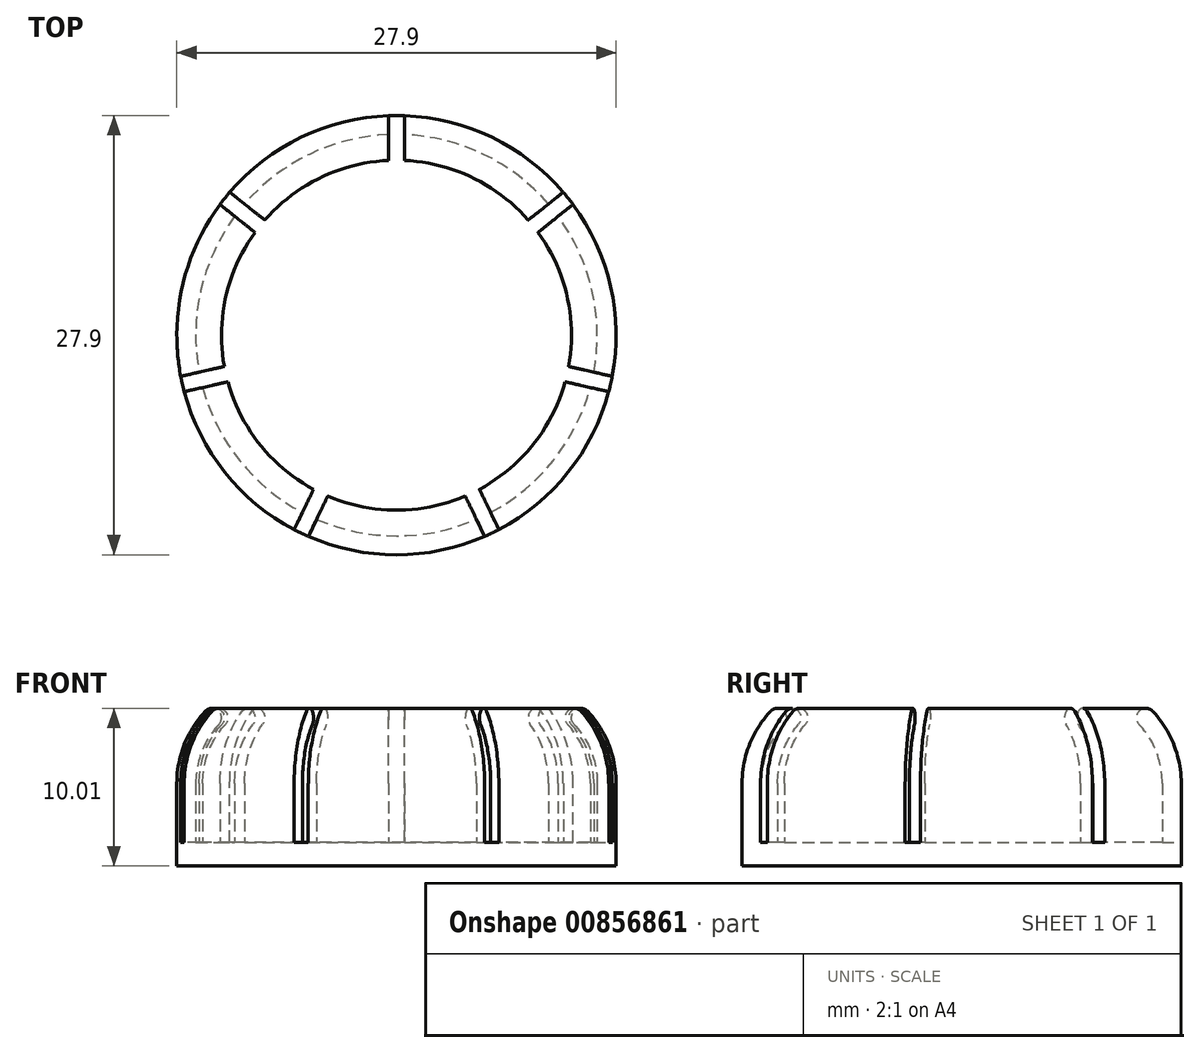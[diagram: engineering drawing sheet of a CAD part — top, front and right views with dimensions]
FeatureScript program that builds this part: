
annotation { "Feature Type Name" : "Feature", "Feature Type Description" : "" }
export const myFeature = defineFeature(function(context is Context, id is Id, definition is map)
    precondition{}
    {
        {
            var Q0;
            Q0=qCreatedBy(makeId("Top.planeOp"),FACE);
            var sketch = newSketch(context, id + "F0", { "sketchPlane" : qUnion([Q0])});
            skCircle(sketch, "E0", {"center": v(0, 0) * mm, "radius": 12.75 * mm});
            skSolve(sketch);
        }
        {
            var Q0;
            Q0=qCreatedBy(makeId("Front.planeOp"),FACE);
            var sketch = newSketch(context, id + "F1", { "sketchPlane" : qUnion([Q0])});
            skArc(sketch, "E1", {"start": v(12.75, 3.75) * mm, "mid": v(12.37, 5.77) * mm, "end": v(11.27, 7.5) * mm});
            skPoint(sketch, "E2", {"position": v(12.75, 0) * mm});
            skLineSegment(sketch, "E3", {"start": v(12.75, 0) * mm, "end": v(12.75, 3.75) * mm});
            skLineSegment(sketch, "E4", {"start": v(0, 0) * mm, "end": v(0, 7.5) * mm, "construction": true});
            skPoint(sketch, "E5", {"position": v(0, 3.75) * mm});
            skArc(sketch, "E6.0", {"start": v(13.95, 3.75) * mm, "mid": v(13.48, 6.2) * mm, "end": v(12.15, 8.32) * mm});
            skLineSegment(sketch, "E6.1", {"start": v(13.95, 0) * mm, "end": v(13.95, 3.75) * mm});
            skLineSegment(sketch, "E7", {"start": v(12.75, 0) * mm, "end": v(13.95, 0) * mm});
            skLineSegment(sketch, "E8", {"start": v(7.25, 3.75) * mm, "end": v(12.15, 8.32) * mm, "construction": true});
            skArc(sketch, "E9", {"start": v(12.15, 8.32) * mm, "mid": v(11.3, 8.35) * mm, "end": v(11.27, 7.5) * mm});
            skSolve(sketch);
        }
        {
            var Q0;
            Q0=makeQuery(id+"F1.imprint","IMPRINT",FACE,{"disambiguationData":[TD([[makeQuery(id+"F1.imprint","IMPRINT",EDGE,{"derivedFrom":sQuery(id+"F1.wireOp",EDGE,"E1")}),-1.0]])]});
            var Q1;
            Q1=sQuery(id+"F1.wireOp",EDGE,"E4");
            revolve(context, id + "F2", {"surfaceOperationType" : NewSurfaceOperationType.NEW, "entities" : qUnion([Q0]), "axis" : qUnion([Q1]), "revolveType" : RevolveType.FULL});
        }
        {
            var Q0;
            Q0=makeQuery(id+"F2.opRevolve","SWEPT_FACE",FACE,{"disambiguationData":[OSD([sQuery(id+"F1.wireOp",EDGE,"E7")])]});
            var sketch = newSketch(context, id + "F3", { "sketchPlane" : qUnion([Q0])});
            skCircle(sketch, "E10.0", {"center": v(0, 0) * mm, "radius": 13.95 * mm});
            skSolve(sketch);
        }
        {
            var Q0;
            Q0 = qSketchRegion(id + "F3", true);
            extrude(context, id + "F4", {"entities" : qUnion([Q0]), "operationType" : NewBodyOperationType.ADD, "depth" : 1.5 * mm, "offsetDistance" : 25 * mm});
        }
        {
            var Q0;
            Q0=makeQuery(id+"F0.imprint","IMPRINT",FACE,{"disambiguationData":[TD([[makeQuery(id+"F0.imprint","IMPRINT",EDGE,{"derivedFrom":sQuery(id+"F0.wireOp",EDGE,"E0")}),1.0]])]});
            var sketch = newSketch(context, id + "F5", { "sketchPlane" : qUnion([Q0])});
            skLineSegment(sketch, "E11.bottom", {"start": v(0.5, 10.35) * mm, "end": v(-0.5, 10.35) * mm});
            skLineSegment(sketch, "E11.top", {"start": v(0.5, 13.95) * mm, "end": v(-0.5, 13.95) * mm});
            skLineSegment(sketch, "E11.left", {"start": v(0.5, 10.35) * mm, "end": v(0.5, 13.95) * mm});
            skLineSegment(sketch, "E11.right", {"start": v(-0.5, 10.35) * mm, "end": v(-0.5, 13.95) * mm});
            skPoint(sketch, "E11.middle", {"position": v(0, 12.15) * mm});
            skLineSegment(sketch, "E12.1.0", {"start": v(-7.78, 6.85) * mm, "end": v(-10.6, 9.09) * mm});
            skLineSegment(sketch, "E12.1.1", {"start": v(-10.6, 9.09) * mm, "end": v(-11.22, 8.3) * mm});
            skLineSegment(sketch, "E12.1.2", {"start": v(-8.4, 6.06) * mm, "end": v(-11.22, 8.3) * mm});
            skLineSegment(sketch, "E12.1.3", {"start": v(-7.78, 6.85) * mm, "end": v(-8.4, 6.06) * mm});
            skLineSegment(sketch, "E12.2.0", {"start": v(-10.2, -1.82) * mm, "end": v(-13.71, -2.62) * mm});
            skLineSegment(sketch, "E12.2.1", {"start": v(-13.71, -2.62) * mm, "end": v(-13.49, -3.6) * mm});
            skLineSegment(sketch, "E12.2.2", {"start": v(-9.98, -2.8) * mm, "end": v(-13.49, -3.6) * mm});
            skLineSegment(sketch, "E12.2.3", {"start": v(-10.2, -1.82) * mm, "end": v(-9.98, -2.8) * mm});
            skLineSegment(sketch, "E12.3.0", {"start": v(-4.94, -9.11) * mm, "end": v(-6.5, -12.35) * mm});
            skLineSegment(sketch, "E12.3.1", {"start": v(-6.5, -12.35) * mm, "end": v(-5.6, -12.79) * mm});
            skLineSegment(sketch, "E12.3.2", {"start": v(-4.04, -9.54) * mm, "end": v(-5.6, -12.79) * mm});
            skLineSegment(sketch, "E12.3.3", {"start": v(-4.94, -9.11) * mm, "end": v(-4.04, -9.54) * mm});
            skLineSegment(sketch, "E12.4.0", {"start": v(4.04, -9.54) * mm, "end": v(5.6, -12.79) * mm});
            skLineSegment(sketch, "E12.4.1", {"start": v(5.6, -12.79) * mm, "end": v(6.5, -12.35) * mm});
            skLineSegment(sketch, "E12.4.2", {"start": v(4.94, -9.11) * mm, "end": v(6.5, -12.35) * mm});
            skLineSegment(sketch, "E12.4.3", {"start": v(4.04, -9.54) * mm, "end": v(4.94, -9.11) * mm});
            skLineSegment(sketch, "E12.5.0", {"start": v(9.98, -2.8) * mm, "end": v(13.49, -3.6) * mm});
            skLineSegment(sketch, "E12.5.1", {"start": v(13.49, -3.6) * mm, "end": v(13.71, -2.62) * mm});
            skLineSegment(sketch, "E12.5.2", {"start": v(10.2, -1.82) * mm, "end": v(13.71, -2.62) * mm});
            skLineSegment(sketch, "E12.5.3", {"start": v(9.98, -2.8) * mm, "end": v(10.2, -1.82) * mm});
            skLineSegment(sketch, "E12.6.0", {"start": v(8.4, 6.06) * mm, "end": v(11.22, 8.3) * mm});
            skLineSegment(sketch, "E12.6.1", {"start": v(11.22, 8.3) * mm, "end": v(10.6, 9.09) * mm});
            skLineSegment(sketch, "E12.6.2", {"start": v(7.78, 6.85) * mm, "end": v(10.6, 9.09) * mm});
            skLineSegment(sketch, "E12.6.3", {"start": v(8.4, 6.06) * mm, "end": v(7.78, 6.85) * mm});
            skPoint(sketch, "E12.center", {"position": v(0, 0) * mm});
            skSolve(sketch);
        }
        {
            var Q0;
            Q0 = qSketchRegion(id + "F5", true);
            extrude(context, id + "F6", {"entities" : qUnion([Q0]), "operationType" : NewBodyOperationType.REMOVE, "depth" : 10 * mm, "offsetDistance" : 25 * mm});
        }
    });
